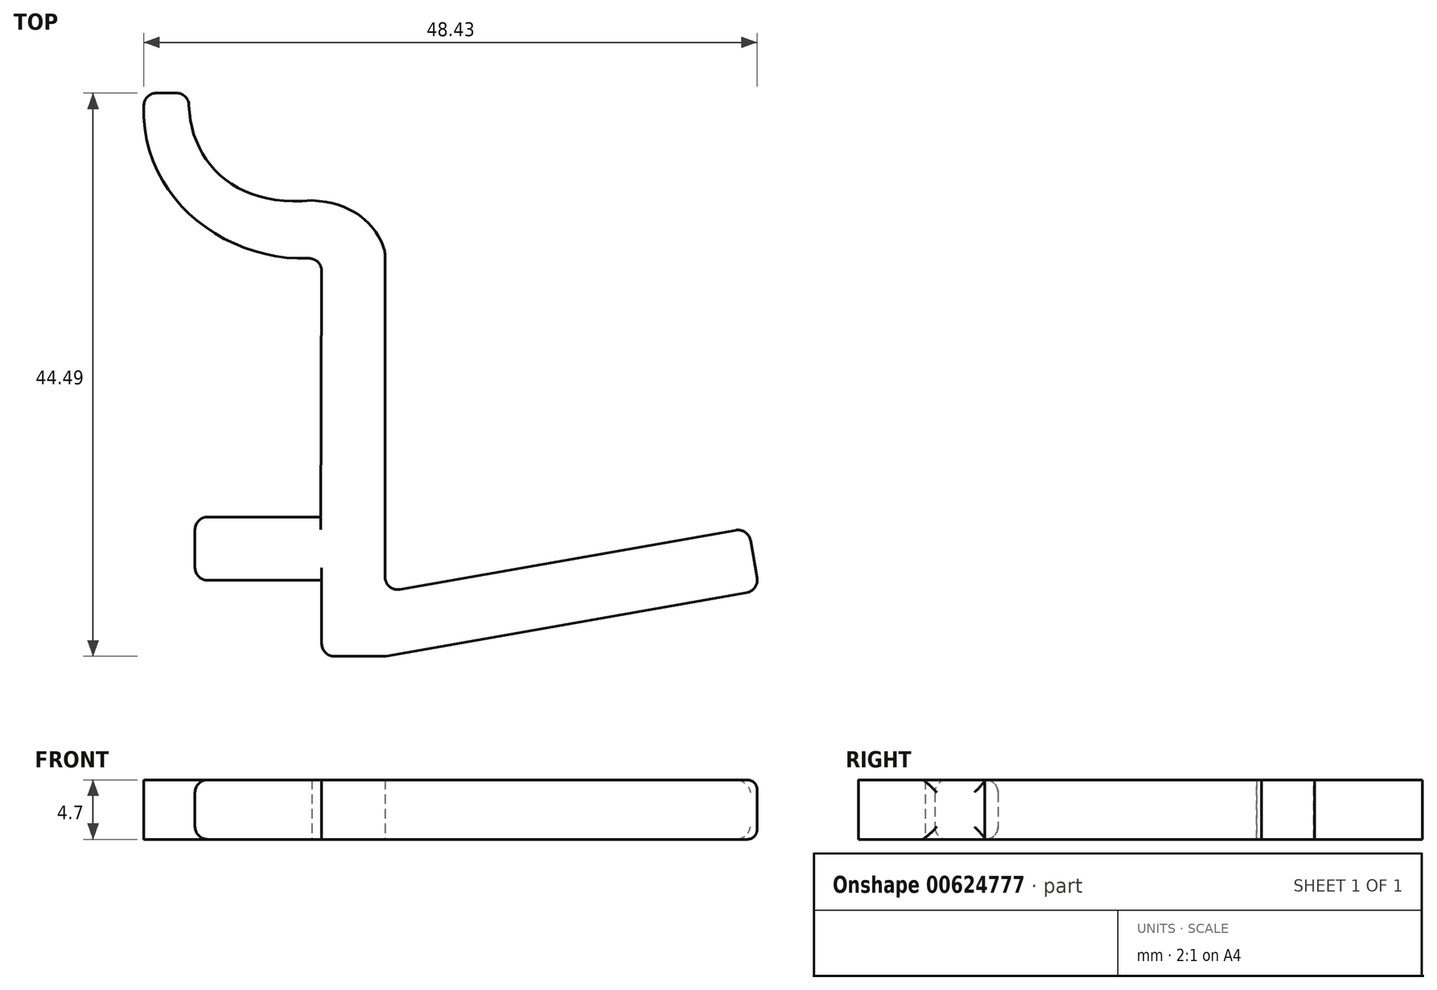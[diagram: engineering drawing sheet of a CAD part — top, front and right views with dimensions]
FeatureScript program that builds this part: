
annotation { "Feature Type Name" : "Feature", "Feature Type Description" : "" }
export const myFeature = defineFeature(function(context is Context, id is Id, definition is map)
    precondition{}
    {
        {
            var Q0;
            Q0=qCreatedBy(makeId("Top.planeOp"),FACE);
            var sketch = newSketch(context, id + "F0", { "sketchPlane" : qUnion([Q0])});
            skLineSegment(sketch, "E0", {"start": v(-41.36, 16.6) * mm, "end": v(-37.86, 16.6) * mm});
            skFitSpline(sketch, "E1", {"points": [v(-37.86, 16.6) * mm, v(-28.18, 8.11) * mm], "startDerivative": vector(-1.06, -15.17) * mm, "endDerivative": vector(19.05, 1.96) * mm});
            skFitSpline(sketch, "E2", {"points": [v(-28.18, 8.11) * mm, v(-22.4, 3.9) * mm], "startDerivative": vector(13.6, -0.54) * mm, "endDerivative": vector(0.17, -2.2) * mm});
            skFitSpline(sketch, "E3", {"points": [v(-41.36, 16.6) * mm, v(-27.4, 3.61) * mm], "startDerivative": vector(-2.9, -24.56) * mm, "endDerivative": vector(21.9, 2.52) * mm});
            skLineSegment(sketch, "E4", {"start": v(-22.4, 3.9) * mm, "end": v(-22.4, -27.9) * mm});
            skLineSegment(sketch, "E5", {"start": v(-22.4, -27.9) * mm, "end": v(-27.4, -27.9) * mm});
            skLineSegment(sketch, "E6", {"start": v(-27.4, -27.9) * mm, "end": v(-27.4, -21.89) * mm});
            skLineSegment(sketch, "E7", {"start": v(-27.4, -21.89) * mm, "end": v(-37.4, -21.89) * mm});
            skLineSegment(sketch, "E8", {"start": v(-37.4, -21.89) * mm, "end": v(-37.4, -16.89) * mm});
            skLineSegment(sketch, "E9", {"start": v(-37.4, -16.89) * mm, "end": v(-27.47, -16.89) * mm});
            skLineSegment(sketch, "E10", {"start": v(-27.47, -16.89) * mm, "end": v(-27.4, 3.61) * mm});
            skLineSegment(sketch, "E11", {"start": v(-22.4, -27.9) * mm, "end": v(7.14, -22.69) * mm});
            skLineSegment(sketch, "E12", {"start": v(7.14, -22.69) * mm, "end": v(6.27, -17.76) * mm});
            skLineSegment(sketch, "E13", {"start": v(6.27, -17.76) * mm, "end": v(-22.4, -22.82) * mm});
            skSolve(sketch);
        }
        {
            var Q0;
            Q0=qSketchRegion(id+"F0",true);
            extrude(context, id + "F1", {"entities" : qUnion([Q0]), "depth" : 4.7 * mm, "offsetDistance" : 25 * mm});
        }
        {
            var Q0;
            Q0=makeQuery(id+"F1.opExtrude","CAP_EDGE",EDGE,{"disambiguationData":[OSD([sQuery(id+"F0.wireOp",EDGE,"E9")])],"isStart":false});
            var Q1;
            Q1=makeQuery(id+"F1.opExtrude","CAP_EDGE",EDGE,{"disambiguationData":[OSD([sQuery(id+"F0.wireOp",EDGE,"E9")])],"isStart":true});
            var Q2;
            Q2=makeQuery(id+"F1.opExtrude","CAP_EDGE",EDGE,{"disambiguationData":[OSD([sQuery(id+"F0.wireOp",EDGE,"E7")])],"isStart":false});
            var Q3;
            Q3=makeQuery(id+"F1.opExtrude","CAP_EDGE",EDGE,{"disambiguationData":[OSD([sQuery(id+"F0.wireOp",EDGE,"E7")])],"isStart":true});
            fillet(context, id + "F2", {"entities" : qUnion([Q0, Q1, Q2, Q3]), "radius" : 1 * mm, "tangentPropagation" : true, "allowEdgeOverflow" : false});
        }
        {
            var Q0;
            Q0=makeQuery(id+"F1.opExtrude","SWEPT_EDGE",EDGE,{"disambiguationData":[OSD([sQuery(id+"F0.wireOp",EDGE,"E5"),sQuery(id+"F0.wireOp",EDGE,"E6")])]});
            var Q1;
            Q1=makeQuery(id+"F1.opExtrude","SWEPT_EDGE",EDGE,{"disambiguationData":[OSD([sQuery(id+"F0.wireOp",EDGE,"E3"),sQuery(id+"F0.wireOp",EDGE,"E10")])]});
            fillet(context, id + "F3", {"entities" : qUnion([Q0, Q1]), "radius" : 1 * mm, "tangentPropagation" : true, "allowEdgeOverflow" : false});
        }
        {
            var Q0;
            Q0=makeQuery(id+"F1.opExtrude","SWEPT_EDGE",EDGE,{"disambiguationData":[OSD([sQuery(id+"F0.wireOp",EDGE,"E0"),sQuery(id+"F0.wireOp",EDGE,"E3")])]});
            var Q1;
            Q1=makeQuery(id+"F1.opExtrude","SWEPT_EDGE",EDGE,{"disambiguationData":[OSD([sQuery(id+"F0.wireOp",EDGE,"E0"),sQuery(id+"F0.wireOp",EDGE,"E1")])]});
            fillet(context, id + "F4", {"entities" : qUnion([Q0, Q1]), "radius" : 1 * mm, "tangentPropagation" : true, "allowEdgeOverflow" : false});
        }
        {
            var Q0;
            Q0=makeQuery(id+"F1.opExtrude","SWEPT_EDGE",EDGE,{"disambiguationData":[OSD([sQuery(id+"F0.wireOp",EDGE,"E4"),sQuery(id+"F0.wireOp",EDGE,"E13")])]});
            var Q1;
            Q1=makeQuery(id+"F1.opExtrude","SWEPT_EDGE",EDGE,{"disambiguationData":[OSD([sQuery(id+"F0.wireOp",EDGE,"E12"),sQuery(id+"F0.wireOp",EDGE,"E13")])]});
            var Q2;
            Q2=makeQuery(id+"F1.opExtrude","SWEPT_EDGE",EDGE,{"disambiguationData":[OSD([sQuery(id+"F0.wireOp",EDGE,"E11"),sQuery(id+"F0.wireOp",EDGE,"E12")])]});
            var Q3;
            Q3=makeQuery(id+"F1.opExtrude","CAP_EDGE",EDGE,{"disambiguationData":[OSD([sQuery(id+"F0.wireOp",EDGE,"E12")])],"isStart":true});
            var Q4;
            Q4=makeQuery(id+"F1.opExtrude","CAP_EDGE",EDGE,{"disambiguationData":[OSD([sQuery(id+"F0.wireOp",EDGE,"E12")])],"isStart":false});
            fillet(context, id + "F5", {"entities" : qUnion([Q0, Q1, Q2, Q3, Q4]), "radius" : 1 * mm, "tangentPropagation" : true, "allowEdgeOverflow" : false});
        }
        {
            var Q0;
            Q0=makeQuery(id+"F1.opExtrude","SWEPT_FACE",FACE,{"disambiguationData":[OSD([sQuery(id+"F0.wireOp",EDGE,"E8")])]});
            fillet(context, id + "F6", {"entities" : qUnion([Q0]), "radius" : 1 * mm, "tangentPropagation" : true, "allowEdgeOverflow" : false});
        }
        {
            var Q0;
            Q0=makeQuery(id+"F1.opExtrude","SWEPT_EDGE",EDGE,{"disambiguationData":[OSD([sQuery(id+"F0.wireOp",EDGE,"E4"),sQuery(id+"F0.wireOp",EDGE,"E5"),sQuery(id+"F0.wireOp",EDGE,"E11")])]});
            fillet(context, id + "F7", {"entities" : qUnion([Q0]), "radius" : 1 * mm, "tangentPropagation" : true, "allowEdgeOverflow" : false});
        }
    });
